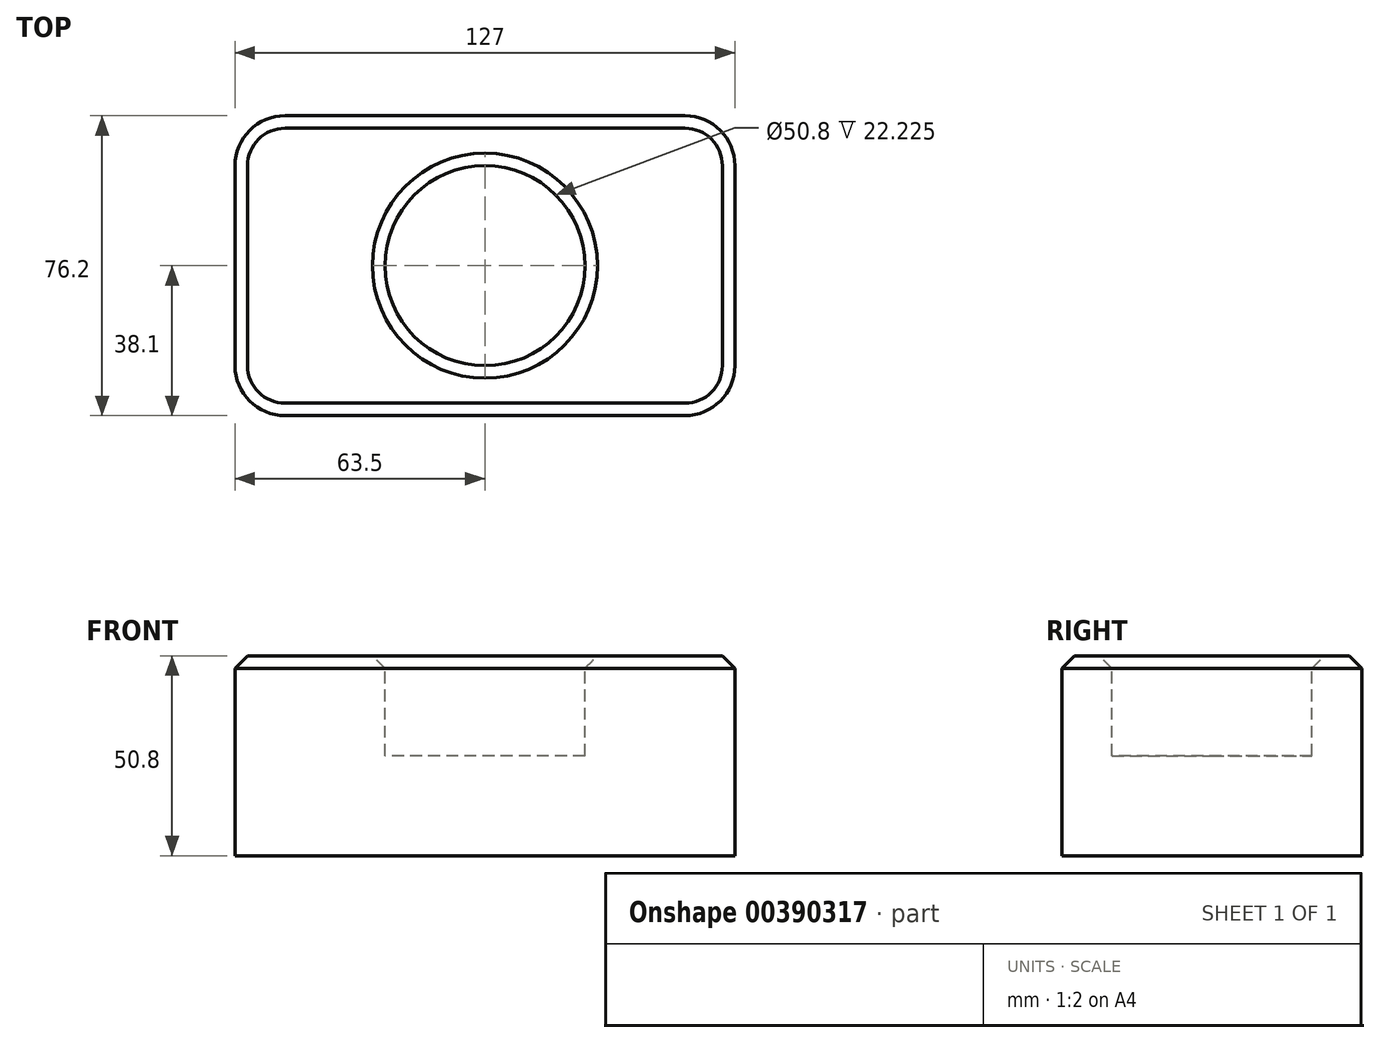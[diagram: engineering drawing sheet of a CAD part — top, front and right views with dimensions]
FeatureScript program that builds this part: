
annotation { "Feature Type Name" : "Feature", "Feature Type Description" : "" }
export const myFeature = defineFeature(function(context is Context, id is Id, definition is map)
    precondition{}
    {
        {
            var Q0;
            Q0=qCreatedBy(makeId("Top.planeOp"),FACE);
            var sketch = newSketch(context, id + "F0", { "sketchPlane" : qUnion([Q0])});
            skLineSegment(sketch, "E0.bottom", {"start": v(63.5, 38.1) * mm, "end": v(-63.5, 38.1) * mm});
            skLineSegment(sketch, "E0.top", {"start": v(63.5, -38.1) * mm, "end": v(-63.5, -38.1) * mm});
            skLineSegment(sketch, "E0.left", {"start": v(63.5, 38.1) * mm, "end": v(63.5, -38.1) * mm});
            skLineSegment(sketch, "E0.right", {"start": v(-63.5, 38.1) * mm, "end": v(-63.5, -38.1) * mm});
            skPoint(sketch, "E0.middle", {"position": v(0, 0) * mm});
            skSolve(sketch);
        }
        {
            var Q0;
            Q0 = qSketchRegion(id + "F0", true);
            extrude(context, id + "F1", {"entities" : qUnion([Q0]), "depth" : 50.8 * mm});
        }
        {
            var Q0;
            Q0=makeQuery(id+"F1.opExtrude","CAP_FACE",FACE,{"disambiguationData":[OSD([sQuery(id+"F0.wireOp",EDGE,"E0.bottom"),sQuery(id+"F0.wireOp",EDGE,"E0.top"),sQuery(id+"F0.wireOp",EDGE,"E0.left"),sQuery(id+"F0.wireOp",EDGE,"E0.right")])],"isStart":false});
            var sketch = newSketch(context, id + "F2", { "sketchPlane" : qUnion([Q0])});
            skCircle(sketch, "E1", {"center": v(0, 0) * mm, "radius": 25.4 * mm});
            skLineSegment(sketch, "E2", {"start": v(-63.5, 38.1) * mm, "end": v(63.5, -38.1) * mm, "construction": true});
            skSolve(sketch);
        }
        {
            var Q0;
            Q0=makeQuery(id+"F2.imprint","IMPRINT",FACE,{"disambiguationData":[TD([[makeQuery(id+"F2.imprint","IMPRINT",EDGE,{"derivedFrom":sQuery(id+"F2.wireOp",EDGE,"E1")}),1.0]])]});
            var Q1;
            Q1=sQuery(id+"F2.wireOp",EDGE,"E1");
            extrude(context, id + "F3", {"entities" : qUnion([Q0]), "operationType" : NewBodyOperationType.REMOVE, "surfaceEntities" : qUnion([Q1]), "oppositeDirection" : true, "depth" : 25.4 * mm});
        }
        {
            var Q0;
            Q0=makeQuery(id+"F1.opExtrude","SWEPT_EDGE",EDGE,{"disambiguationData":[OSD([sQuery(id+"F0.wireOp",EDGE,"E0.top"),sQuery(id+"F0.wireOp",EDGE,"E0.right")])]});
            var Q1;
            Q1=makeQuery(id+"F1.opExtrude","SWEPT_EDGE",EDGE,{"disambiguationData":[OSD([sQuery(id+"F0.wireOp",EDGE,"E0.top"),sQuery(id+"F0.wireOp",EDGE,"E0.left")])]});
            var Q2;
            Q2=makeQuery(id+"F1.opExtrude","SWEPT_EDGE",EDGE,{"disambiguationData":[OSD([sQuery(id+"F0.wireOp",EDGE,"E0.bottom"),sQuery(id+"F0.wireOp",EDGE,"E0.left")])]});
            var Q3;
            Q3=makeQuery(id+"F1.opExtrude","SWEPT_EDGE",EDGE,{"disambiguationData":[OSD([sQuery(id+"F0.wireOp",EDGE,"E0.bottom"),sQuery(id+"F0.wireOp",EDGE,"E0.right")])]});
            fillet(context, id + "F4", {"entities" : qUnion([Q0, Q1, Q2, Q3]), "radius" : 12.7 * mm, "tangentPropagation" : true, "allowEdgeOverflow" : false});
        }
        {
            var Q0;
            Q0=makeQuery(id+"F1.opExtrude","CAP_FACE",FACE,{"disambiguationData":[OSD([sQuery(id+"F0.wireOp",EDGE,"E0.bottom"),sQuery(id+"F0.wireOp",EDGE,"E0.top"),sQuery(id+"F0.wireOp",EDGE,"E0.left"),sQuery(id+"F0.wireOp",EDGE,"E0.right")])],"isStart":false});
            chamfer(context, id + "F5", {"entities" : qUnion([Q0]), "width" : 3.17 * mm, "tangentPropagation" : true});
        }
    });
